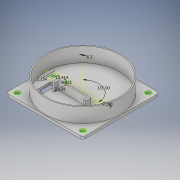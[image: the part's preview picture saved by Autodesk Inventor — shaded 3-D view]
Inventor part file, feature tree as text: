
AUTODESK INVENTOR PART (.ipt)
format: ipt  version: 2019 (Build 230136000, 136)  size: 241,152 bytes
history: native  units: in
note: dims shown in document units (in); Inventor stores cm internally (conversion verified against a paired STEP export)
features: other x9, extrude x7
ambient origin geometry x8: Origin, YZ Plane, XZ Plane, XY Plane, X Axis, Y Axis, Z Axis, Center Point
bodies: Solid1 (feature_tree)
feature tree (16):
  other  "Bottom Base"
  extrude  "Outer Wall Extr"  Depth=3.5in
  extrude  "Base Mount"  Depth=0.122in
  extrude  "Silicon Hole"  Depth=1.83in
  extrude  "HX711 - MCU Hole"  Depth=1.83in
  other  "hx711 mount"
  other  "Bottom Circles"
  extrude  "Bottom Holes"  TaperAngle=90.0deg  [1 undecoded]
  extrude  "Base to Rail Mount"  Depth=3.5in
  extrude  "hx711 walls"  Depth=0.7in TaperAngle=0.0deg
  other  "Bottom"
  other  "Outer Wall Circles"
  other  "Mount Square"
  other  "Silicon Circles"
  other  "HX711-MCU Design"
  other  "Top Shadow"
note: 1 required parameter value undecoded (feature->parameter linkage not recoverable at this tier; creation-order binding heuristic only, values carry confidence <= 0.55)
